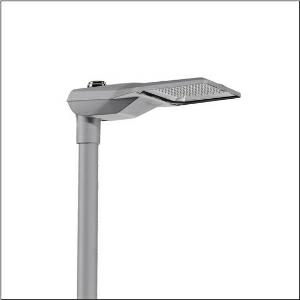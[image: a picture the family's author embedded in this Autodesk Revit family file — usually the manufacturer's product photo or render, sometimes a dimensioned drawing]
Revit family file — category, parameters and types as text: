
# Revit family: streetlight_sl_21_midi___p1_0a_5xe7a37n08mb_bed1
name_source: partatom
category: Lighting Fixtures
units: mm (PartAtom-declared; Revit-internal decimal feet)

## family parameters
Cut with Voids When Loaded = No
Host = Face
Light Source = No
Part Type = Normal
Room Calculation Point = No
Round Connector Dimension = Use Diameter
Shared = No

## types (1)
- --- (1 x LED, 18270 lm, 136 W, 3000K)
    Apparent Load = 136 VA
    CIE Flux Codes = 21 50 90 100 100
    Color Rendering = 70
    Color Temperature = 3000K
    Default Elevation = 1800 mm
    Description = Streetlight SL 21 midi, mast luminaire, primary light control with lens, of PMMA, primary optical cover: cover, of toughened safety glass, transparent, light distribution: P1.0a, light emission: direct distribution, primary light characteristic: asymmetric, installation type: side-entry, LED, 3G 2.5mm², High Power LED, rated luminous flux: 18.270lm, luminous efficacy: 134lm/W, light colour: 730, colour temperature: 3000K, control gear: NEMA (7pin), control: overheat protection, pre-setting: linear dimming characteristic, constant luminous flux control, time-dependent luminous flux control, flexible luminous flux parameterisation, mains connection: 220..240V, AC, 50/60Hz, connection cable pre-assembled, cable length: 12,5m, wiring characteristics: H05VV-F, start of lifetime: 136W, end of service life: 142W, reduction: 61W, luminaire housing, of diecast aluminium (EN AC-44300), powder-coated, SITECO metallic grey (DB 702S), corrosivity category C5 high according to DIN EN ISO 12944, multi-level sealing system, sealing non-destructively replaceable, inclination adjustable: 0°, 5°, 10°, 15°, length: 644mm, width: 335mm, height: 110mm, spigot size: 42mm (side-entry), mounting height: 4..8m, protection rating (complete): IP66, insulation class (complete): insulation class I (protective earthing), certification: CE, ENEC, ENEC+, VDE, impact resistance: IK10, permissible operating ambient temperature for outdoor applications: -40..+50°C, standard-compliant lighting for roads and squares, packaging unit: 1 piece

Light Distribution: P1.0a
    Height = 111 mm
    Lamp = 1 x LED
    Lamp Light Flux = 18270 lm
    Lamp Power = 136 W
    Lamp count = 1
    Length = 644 mm
    Luminous efficacy = 134 lm/W
    Manufacturer = Siteco
    ModVariant = No
    Model = 5XE7A37N08MB
    Number of Poles = 1
    OnlyDefault = Yes
    Power Factor = 1
    Product Name = Streetlight SL 21 midi | P1.0a
    Product group = mast luminaire | pylon top
    ProductGroupID = 6100
    Protection Class = Protection class I
    Protection Degree = IP 66
    RLX_Detail_Level = 1
    RLX_Emergency_Light_Flux = 0 lm
    RLX_Emergency_Type = 0
    RLX_Emergency_Type_DB = No
    RlxData = <blob elided: 37773 chars, md5=9ef824b7>
    Socket = socket
    Standby Power = 0 W
    System Light Flux = 18270 lm
    System Power = 136 W
    Type Comments = factory setting: luminous flux: 100 % | dim-lin: 254 | 695 mA
    Type Image = l_1294377.jpg
    URL = http://relux.com
    VarID = @adj_134017
    Voltage = 0 V
    Weight = 0.00 kg
    Width = 336 mm

## geometry (parser evidence)
native form markers: Blend x4, Sweep x11
no freeform markers — native parametric forms only
